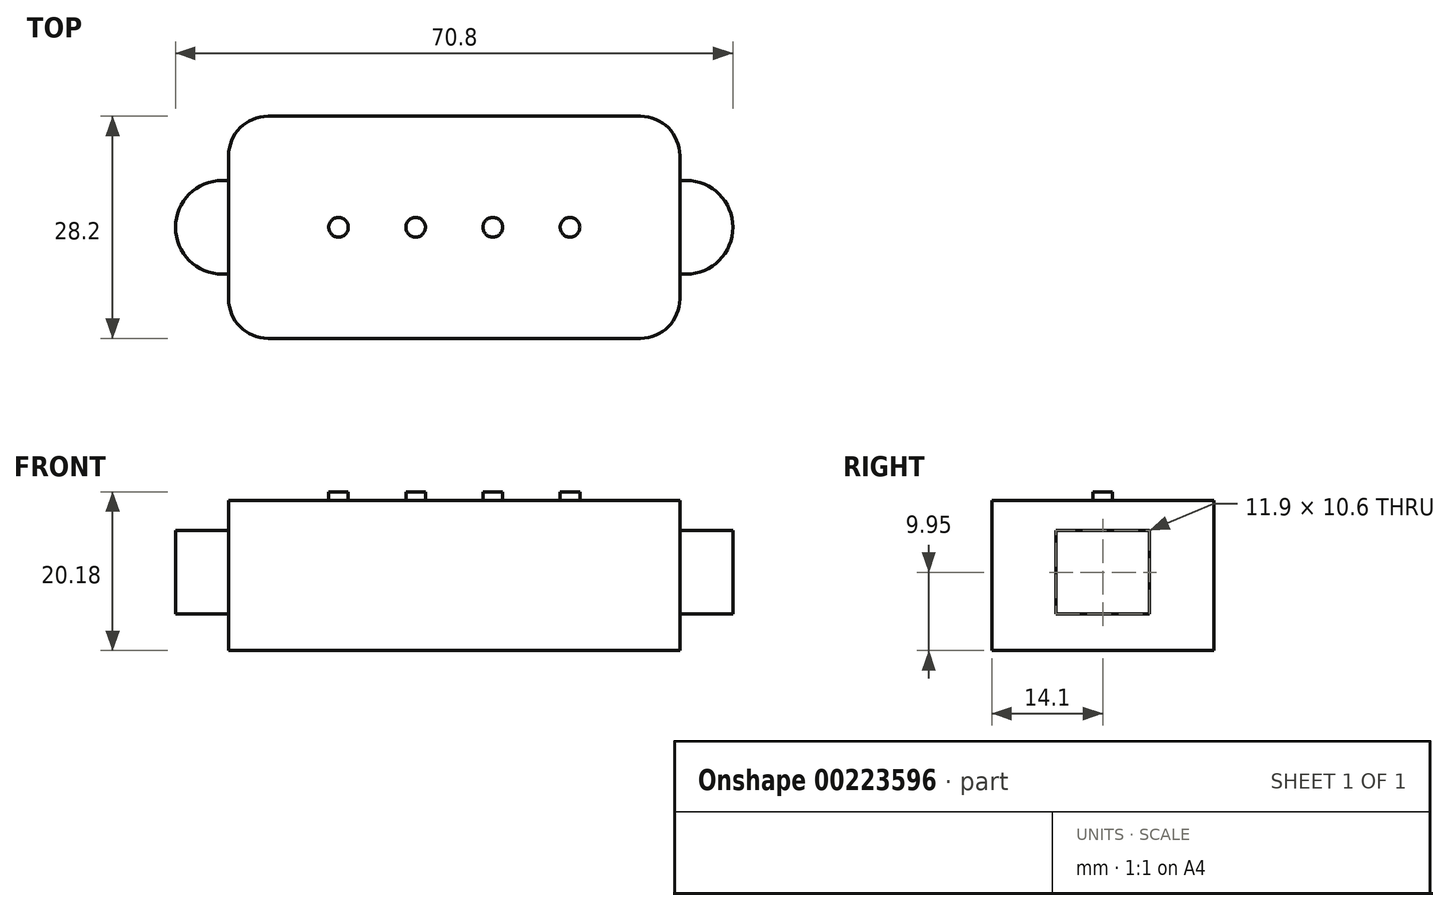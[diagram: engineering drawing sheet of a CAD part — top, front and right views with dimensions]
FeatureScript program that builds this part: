
annotation { "Feature Type Name" : "Feature", "Feature Type Description" : "" }
export const myFeature = defineFeature(function(context is Context, id is Id, definition is map)
    precondition{}
    {
        {
            var Q0;
            Q0=qCreatedBy(makeId("Top.planeOp"),FACE);
            var sketch = newSketch(context, id + "F0", { "sketchPlane" : qUnion([Q0])});
            skLineSegment(sketch, "E0", {"start": v(-28.66, 14.1) * mm, "end": v(28.66, 14.1) * mm});
            skLineSegment(sketch, "E1", {"start": v(-28.66, -14.1) * mm, "end": v(28.66, -14.1) * mm});
            skLineSegment(sketch, "E2", {"start": v(-28.66, 24.11) * mm, "end": v(-28.66, -25.75) * mm, "construction": true});
            skLineSegment(sketch, "E3", {"start": v(28.66, 25.08) * mm, "end": v(28.66, -30.27) * mm, "construction": true});
            skLineSegment(sketch, "E4", {"start": v(-28.66, 14.1) * mm, "end": v(-28.66, -14.1) * mm});
            skLineSegment(sketch, "E5", {"start": v(28.66, 14.1) * mm, "end": v(28.66, -14.1) * mm});
            skSolve(sketch);
        }
        {
            var Q0;
            Q0 = qSketchRegion(id + "F0", true);
            extrude(context, id + "F1", {"entities" : qUnion([Q0]), "depth" : 19.05 * mm});
        }
        {
            var Q0;
            Q0=makeQuery(id+"F1.opExtrude","SWEPT_EDGE",EDGE,{"disambiguationData":[OSD([sQuery(id+"F0.wireOp",EDGE,"E0"),sQuery(id+"F0.wireOp",EDGE,"E4")])]});
            var Q1;
            Q1=makeQuery(id+"F1.opExtrude","SWEPT_EDGE",EDGE,{"disambiguationData":[OSD([sQuery(id+"F0.wireOp",EDGE,"E1"),sQuery(id+"F0.wireOp",EDGE,"E4")])]});
            var Q2;
            Q2=makeQuery(id+"F1.opExtrude","SWEPT_EDGE",EDGE,{"disambiguationData":[OSD([sQuery(id+"F0.wireOp",EDGE,"E1"),sQuery(id+"F0.wireOp",EDGE,"E5")])]});
            var Q3;
            Q3=makeQuery(id+"F1.opExtrude","SWEPT_EDGE",EDGE,{"disambiguationData":[OSD([sQuery(id+"F0.wireOp",EDGE,"E0"),sQuery(id+"F0.wireOp",EDGE,"E5")])]});
            fillet(context, id + "F2", {"entities" : qUnion([Q0, Q1, Q2, Q3]), "radius" : 5 * mm, "tangentPropagation" : true, "allowEdgeOverflow" : false});
        }
        {
            var Q0;
            Q0=makeQuery(id+"F1.opExtrude","CAP_FACE",FACE,{"disambiguationData":[OSD([sQuery(id+"F0.wireOp",EDGE,"E0"),sQuery(id+"F0.wireOp",EDGE,"E1"),sQuery(id+"F0.wireOp",EDGE,"E4"),sQuery(id+"F0.wireOp",EDGE,"E5")])],"isStart":false});
            cPlane(context, id + "F3", {"entities" : qUnion([Q0]), "cplaneType" : CPlaneType.OFFSET, "offset" : 3.8 * mm, "oppositeDirection" : true, "width" : 150 * mm, "height" : 150 * mm});
        }
        {
            var Q0;
            Q0=qCreatedBy(id+"F3.planeOp",FACE);
            var sketch = newSketch(context, id + "F4", { "sketchPlane" : qUnion([Q0])});
            skLineSegment(sketch, "E6", {"start": v(-35.4, 26.19) * mm, "end": v(-35.4, -35.74) * mm, "construction": true});
            skLineSegment(sketch, "E7", {"start": v(35.4, 28.25) * mm, "end": v(35.4, -30.4) * mm, "construction": true});
            skLineSegment(sketch, "E8", {"start": v(-39.8, 5.95) * mm, "end": v(-35.4, 5.95) * mm, "construction": true});
            skLineSegment(sketch, "E9", {"start": v(-40.55, -5.95) * mm, "end": v(-35.4, -5.95) * mm, "construction": true});
            skArc(sketch, "E10", {"start": v(-29.45, 5.95) * mm, "mid": v(-35.4, 0) * mm, "end": v(-29.45, -5.95) * mm});
            skLineSegment(sketch, "E11.trimOffspring", {"start": v(-29.45, 5.95) * mm, "end": v(-27.72, 5.95) * mm});
            skLineSegment(sketch, "E12.trimOffspring", {"start": v(-29.45, -5.95) * mm, "end": v(-27.72, -5.95) * mm});
            skLineSegment(sketch, "E13", {"start": v(-27.72, 5.95) * mm, "end": v(-27.72, -5.95) * mm});
            skLineSegment(sketch, "E14.trimOffspring", {"start": v(35.4, 5.95) * mm, "end": v(40.39, 5.95) * mm});
            skLineSegment(sketch, "E15.trimOffspring", {"start": v(35.4, -5.95) * mm, "end": v(40.85, -5.95) * mm});
            skLineSegment(sketch, "E16.MirrorCS", {"start": v(29.45, -5.95) * mm, "end": v(27.72, -5.95) * mm});
            skLineSegment(sketch, "E17.MirrorCS", {"start": v(29.45, 5.95) * mm, "end": v(27.72, 5.95) * mm});
            skArc(sketch, "E18.MirrorCS", {"start": v(29.45, 5.95) * mm, "mid": v(35.4, 0) * mm, "end": v(29.45, -5.95) * mm});
            skLineSegment(sketch, "E19.MirrorCS", {"start": v(27.72, 5.95) * mm, "end": v(27.72, -5.95) * mm});
            skSolve(sketch);
        }
        {
            var Q0;
            Q0 = qSketchRegion(id + "F4", true);
            extrude(context, id + "F5", {"entities" : qUnion([Q0]), "operationType" : NewBodyOperationType.ADD, "oppositeDirection" : true, "depth" : 10.6 * mm});
        }
        {
            var Q0;
            Q0=makeQuery(id+"F1.opExtrude","CAP_FACE",FACE,{"disambiguationData":[OSD([sQuery(id+"F0.wireOp",EDGE,"E0"),sQuery(id+"F0.wireOp",EDGE,"E1"),sQuery(id+"F0.wireOp",EDGE,"E4"),sQuery(id+"F0.wireOp",EDGE,"E5")])],"isStart":false});
            var sketch = newSketch(context, id + "F6", { "sketchPlane" : qUnion([Q0])});
            skLineSegment(sketch, "E20", {"start": v(-4.9, 9.8) * mm, "end": v(-4.9, -9.26) * mm, "construction": true});
            skLineSegment(sketch, "E21", {"start": v(-14.7, 9.7) * mm, "end": v(-14.7, -9.78) * mm, "construction": true});
            skCircle(sketch, "E22", {"center": v(-14.7, 0) * mm, "radius": 1.25 * mm});
            skCircle(sketch, "E23.1.0.0", {"center": v(-4.9, 0) * mm, "radius": 1.25 * mm});
            skCircle(sketch, "E23.2.0.0", {"center": v(4.9, 0) * mm, "radius": 1.25 * mm});
            skCircle(sketch, "E23.3.0.0", {"center": v(14.7, 0) * mm, "radius": 1.25 * mm});
            skLineSegment(sketch, "E23.direction1", {"start": v(-14.7, 0) * mm, "end": v(-4.9, 0) * mm, "construction": true});
            skSolve(sketch);
        }
        {
            var Q0;
            Q0 = qSketchRegion(id + "F6", true);
            extrude(context, id + "F7", {"entities" : qUnion([Q0]), "operationType" : NewBodyOperationType.ADD, "depth" : 1.13 * mm});
        }
    });
